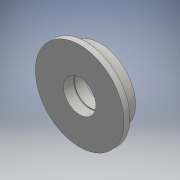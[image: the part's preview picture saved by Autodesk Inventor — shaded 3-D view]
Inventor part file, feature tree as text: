
AUTODESK INVENTOR PART (.ipt)
format: ipt  version: 2016 (Build 200138000, 138)  size: 119,808 bytes
history: native  units: mm
features: extrude x5, sketch x5
ambient origin geometry x8: Origin, YZ Plane, XZ Plane, XY Plane, X Axis, Y Axis, Z Axis, Center Point
bodies: Solid1 (feature_tree)
feature tree (10):
  extrude  "Extrusion1"  Depth=4.0mm TaperAngle=0.0deg
  extrude  "Extrusion2"  Depth=10.0mm
  extrude  "Extrusion3"  Depth=16.0mm TaperAngle=0.0deg
  extrude  "Extrusion4"  Depth=7.0mm TaperAngle=0.0deg
  extrude  "Extrusion5"  Depth=17.0mm TaperAngle=0.0deg
  sketch  "Sketch1"  dims[d0=60.0mm d1=4.0mm d2=0.0mm]
  sketch  "Sketch2"  dims[d3=55.0mm d4=10.0mm d5=-3.490659mm]
  sketch  "Sketch3"  dims[d6=8.0mm d7=16.0mm d8=0.0mm]
  sketch  "Sketch4"  dims[d9=22.0mm d10=7.0mm d11=0.0mm]
  sketch  "Sketch5"  dims[d12=21.0mm d13=17.0mm d14=0.0mm]
